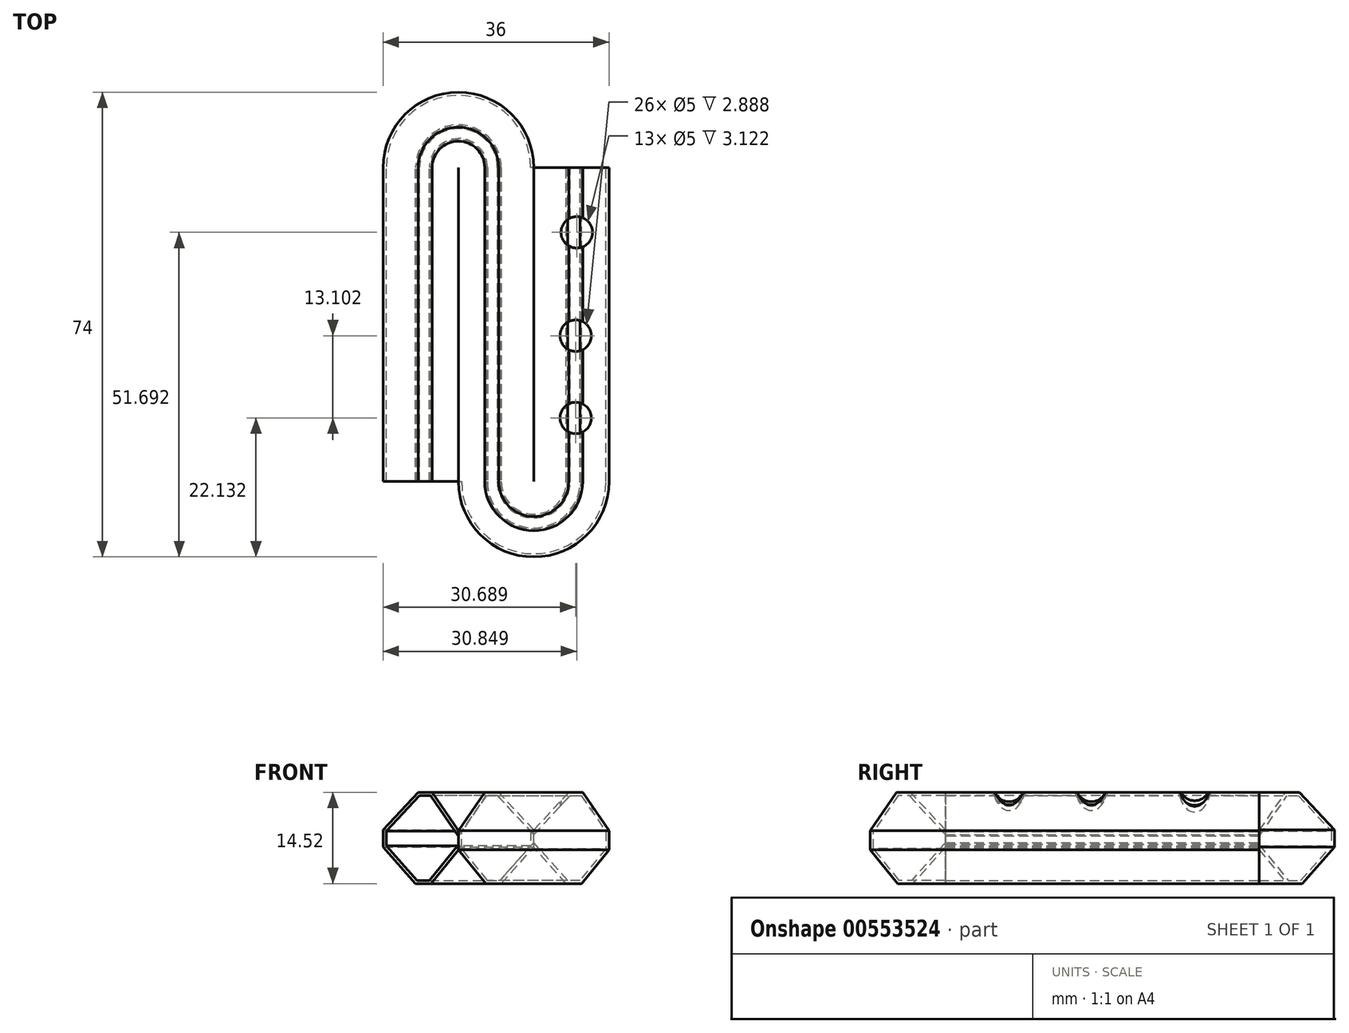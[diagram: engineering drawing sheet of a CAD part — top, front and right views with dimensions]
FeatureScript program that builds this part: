
annotation { "Feature Type Name" : "Feature", "Feature Type Description" : "" }
export const myFeature = defineFeature(function(context is Context, id is Id, definition is map)
    precondition{}
    {
        {
            var Q0;
            Q0=qCreatedBy(makeId("Top.planeOp"),FACE);
            var sketch = newSketch(context, id + "F0", { "sketchPlane" : qUnion([Q0])});
            skLineSegment(sketch, "E0", {"start": v(0, 0) * mm, "end": v(0, 50) * mm});
            skLineSegment(sketch, "E1", {"start": v(0, 50) * mm, "end": v(12, 50) * mm});
            skLineSegment(sketch, "E2", {"start": v(12, 50) * mm, "end": v(12, 0) * mm});
            skLineSegment(sketch, "E3", {"start": v(12, 0) * mm, "end": v(24, 0) * mm});
            skLineSegment(sketch, "E4", {"start": v(24, 0) * mm, "end": v(24, 50) * mm});
            skArc(sketch, "E5", {"start": v(12, 50) * mm, "mid": v(6, 56) * mm, "end": v(0, 50) * mm});
            skArc(sketch, "E6", {"start": v(12, 0) * mm, "mid": v(18, -6) * mm, "end": v(24, 0) * mm});
            skSolve(sketch);
        }
        {
            var Q0;
            Q0=qCreatedBy(makeId("Front.planeOp"),FACE);
            var sketch = newSketch(context, id + "F1", { "sketchPlane" : qUnion([Q0])});
            skLineSegment(sketch, "E7", {"start": v(6, 1.42) * mm, "end": v(6, -1.63) * mm});
            skLineSegment(sketch, "E8", {"start": v(6, -1.63) * mm, "end": v(1.61, -7) * mm});
            skLineSegment(sketch, "E9", {"start": v(1.61, -7) * mm, "end": v(-0.82, -7) * mm});
            skLineSegment(sketch, "E10", {"start": v(-0.82, -7) * mm, "end": v(-6, -1.22) * mm});
            skLineSegment(sketch, "E11", {"start": v(-6, -1.22) * mm, "end": v(-6, 1.52) * mm});
            skLineSegment(sketch, "E12", {"start": v(-6, 1.52) * mm, "end": v(-0.42, 7.51) * mm});
            skLineSegment(sketch, "E13", {"start": v(-0.42, 7.51) * mm, "end": v(1.82, 7.51) * mm});
            skLineSegment(sketch, "E14", {"start": v(1.82, 7.51) * mm, "end": v(6, 1.42) * mm});
            skSolve(sketch);
        }
        {
            var Q0;
            Q0=makeQuery(id+"F1.imprint","IMPRINT",FACE,{"disambiguationData":[TD([[makeQuery(id+"F1.imprint","IMPRINT",EDGE,{"derivedFrom":sQuery(id+"F1.wireOp",EDGE,"E7")}),-1.0]])]});
            var Q1;
            Q1=sQuery(id+"F0.wireOp",EDGE,"E0");
            var Q2;
            Q2=sQuery(id+"F0.wireOp",EDGE,"E5");
            var Q3;
            Q3=sQuery(id+"F0.wireOp",EDGE,"E2");
            var Q4;
            Q4=sQuery(id+"F0.wireOp",EDGE,"E6");
            var Q5;
            Q5=sQuery(id+"F0.wireOp",EDGE,"E4");
            sweep(context, id + "F2", {"profiles" : qUnion([Q0]), "path" : qUnion([Q1, Q2, Q3, Q4, Q5])});
        }
        {
            var Q0;
            Q0=makeQuery(id+"F2.opSweep","CAP_FACE",FACE,{"disambiguationData":[OSD([sQuery(id+"F0.wireOp",VERTEX,"E0.start"),sQuery(id+"F1.wireOp",EDGE,"E7"),sQuery(id+"F1.wireOp",EDGE,"E8"),sQuery(id+"F1.wireOp",EDGE,"E9"),sQuery(id+"F1.wireOp",EDGE,"E10"),sQuery(id+"F1.wireOp",EDGE,"E11"),sQuery(id+"F1.wireOp",EDGE,"E12"),sQuery(id+"F1.wireOp",EDGE,"E13"),sQuery(id+"F1.wireOp",EDGE,"E14")])],"isStart":true});
            var Q1;
            Q1=makeQuery(id+"F2.opSweep","CAP_FACE",FACE,{"disambiguationData":[OSD([sQuery(id+"F0.wireOp",VERTEX,"E4.end"),sQuery(id+"F1.wireOp",EDGE,"E7"),sQuery(id+"F1.wireOp",EDGE,"E8"),sQuery(id+"F1.wireOp",EDGE,"E9"),sQuery(id+"F1.wireOp",EDGE,"E10"),sQuery(id+"F1.wireOp",EDGE,"E11"),sQuery(id+"F1.wireOp",EDGE,"E12"),sQuery(id+"F1.wireOp",EDGE,"E13"),sQuery(id+"F1.wireOp",EDGE,"E14")])],"isStart":false});
            shell(context, id + "F3", {"entities" : qUnion([Q0, Q1]), "thickness" : 0.5 * mm});
        }
        {
            var Q0;
            Q0=qCreatedBy(makeId("Top.planeOp"),FACE);
            var sketch = newSketch(context, id + "F4", { "sketchPlane" : qUnion([Q0])});
            skPoint(sketch, "E15", {"position": v(24.85, 39.7) * mm});
            skPoint(sketch, "E16", {"position": v(24.69, 23.23) * mm});
            skPoint(sketch, "E17", {"position": v(24.69, 10.13) * mm});
            skSolve(sketch);
        }
        {
            var Q0;
            Q0=sQuery(id+"F4.wireOp",VERTEX,"E15");
            var Q1;
            Q1=sQuery(id+"F4.wireOp",VERTEX,"E16");
            var Q2;
            Q2=sQuery(id+"F4.wireOp",VERTEX,"E17");
            var Q3;
            Q3=makeQuery(id+"F2.opSweep","SWEPT_BODY",BODY,{"disambiguationData":[OSD([sQuery(id+"F0.wireOp",EDGE,"E4"),sQuery(id+"F1.wireOp",EDGE,"E7"),sQuery(id+"F1.wireOp",EDGE,"E8"),sQuery(id+"F1.wireOp",EDGE,"E9"),sQuery(id+"F1.wireOp",EDGE,"E10"),sQuery(id+"F1.wireOp",EDGE,"E11"),sQuery(id+"F1.wireOp",EDGE,"E12"),sQuery(id+"F1.wireOp",EDGE,"E13"),sQuery(id+"F1.wireOp",EDGE,"E14")])]});
            hole(context, id + "F5", {"style" : HoleStyle.SIMPLE, "endStyle" : HoleEndStyle.THROUGH, "oppositeDirection" : true, "holeDiameter" : 5 * mm, "isTappedThrough" : true, "tappedDepth" : 12 * mm, "tapClearance" : 3, "locations" : qUnion([Q0, Q1, Q2]), "scope" : qUnion([Q3])});
        }
    });
